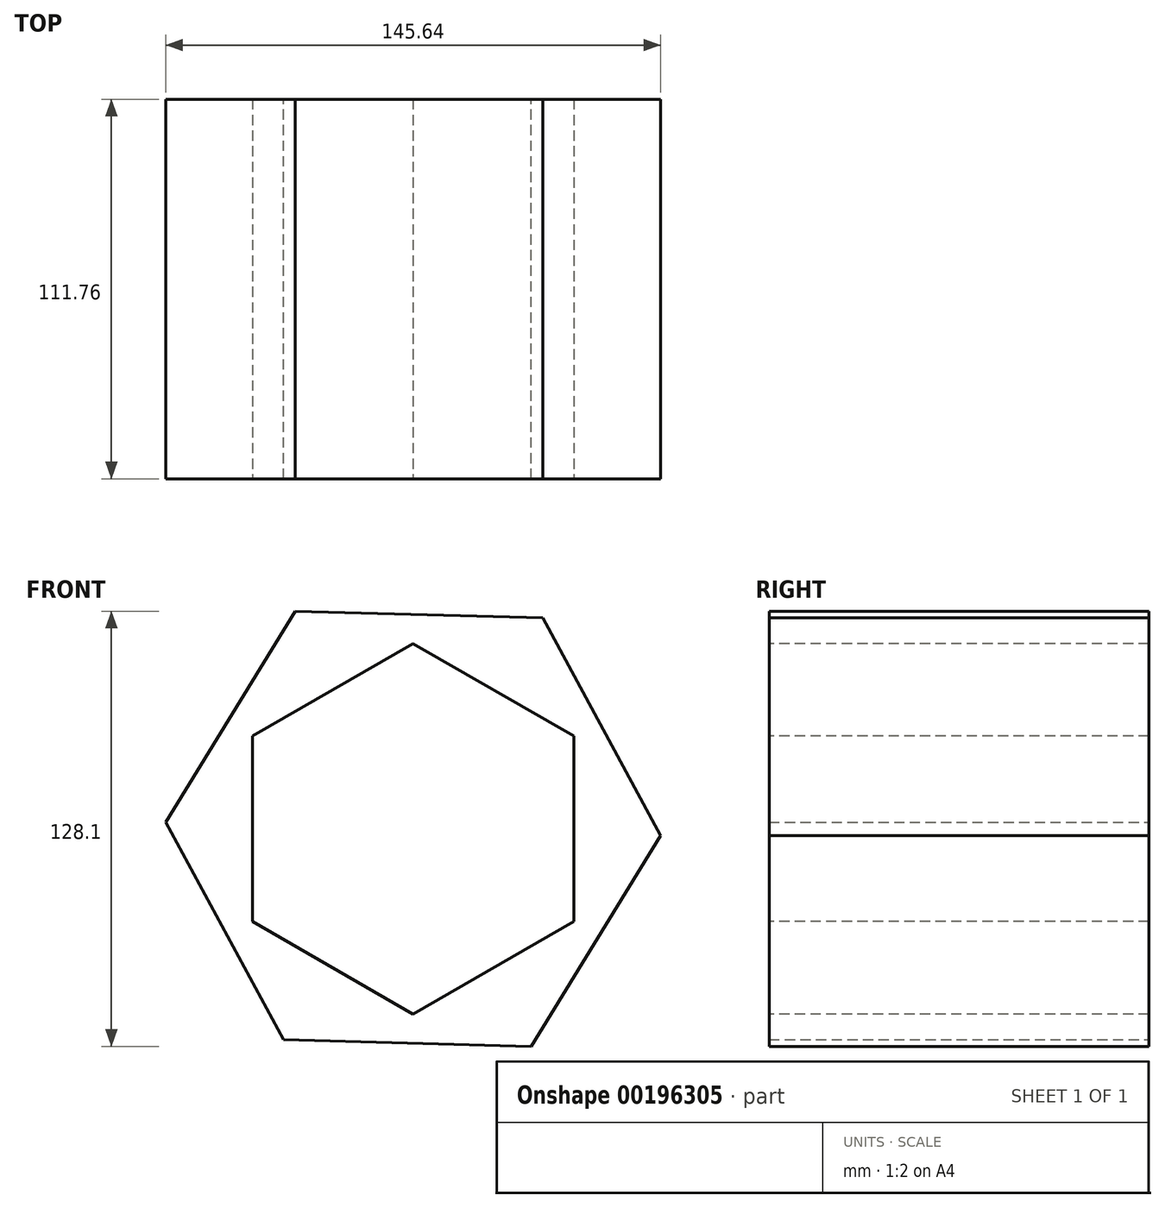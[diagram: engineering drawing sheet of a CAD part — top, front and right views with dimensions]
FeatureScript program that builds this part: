
annotation { "Feature Type Name" : "Feature", "Feature Type Description" : "" }
export const myFeature = defineFeature(function(context is Context, id is Id, definition is map)
    precondition{}
    {
        {
            var Q0;
            Q0=qCreatedBy(makeId("Front.planeOp"),FACE);
            var sketch = newSketch(context, id + "F0", { "sketchPlane" : qUnion([Q0])});
            skCircle(sketch, "E0.cCircle", {"center": v(0, 0) * mm, "radius": 63.09 * mm, "construction": true});
            skLineSegment(sketch, "E0.0", {"start": v(38.11, 62.08) * mm, "end": v(72.82, -1.97) * mm});
            skLineSegment(sketch, "E0.1", {"start": v(72.82, -1.97) * mm, "end": v(34.7, -64.05) * mm});
            skLineSegment(sketch, "E0.2", {"start": v(34.7, -64.05) * mm, "end": v(-38.11, -62.08) * mm});
            skLineSegment(sketch, "E0.3", {"start": v(-38.11, -62.08) * mm, "end": v(-72.82, 1.97) * mm});
            skLineSegment(sketch, "E0.4", {"start": v(-72.82, 1.97) * mm, "end": v(-34.7, 64.05) * mm});
            skLineSegment(sketch, "E0.5", {"start": v(-34.7, 64.05) * mm, "end": v(38.11, 62.08) * mm});
            skPoint(sketch, "E0.0.midPoint", {"position": v(55.47, 30.06) * mm});
            skSolve(sketch);
        }
        {
            var Q0;
            Q0 = qSketchRegion(id + "F0", true);
            extrude(context, id + "F1", {"entities" : qUnion([Q0]), "depth" : 111.76 * mm});
        }
        {
            var Q0;
            Q0=makeQuery(id+"F1.opExtrude","CAP_FACE",FACE,{"disambiguationData":[OSD([sQuery(id+"F0.wireOp",EDGE,"E0.0"),sQuery(id+"F0.wireOp",EDGE,"E0.1"),sQuery(id+"F0.wireOp",EDGE,"E0.2"),sQuery(id+"F0.wireOp",EDGE,"E0.3"),sQuery(id+"F0.wireOp",EDGE,"E0.4"),sQuery(id+"F0.wireOp",EDGE,"E0.5")])],"isStart":false});
            var sketch = newSketch(context, id + "F2", { "sketchPlane" : qUnion([Q0])});
            skCircle(sketch, "E1", {"center": v(0, 0) * mm, "radius": 39.09 * mm});
            skSolve(sketch);
        }
        {
            var Q0;
            Q0=makeQuery(id+"F2.imprint","IMPRINT",FACE,{"disambiguationData":[TD([[makeQuery(id+"F2.imprint","IMPRINT",EDGE,{"derivedFrom":sQuery(id+"F2.wireOp",EDGE,"E1")}),1.0]])]});
            var sketch = newSketch(context, id + "F3", { "sketchPlane" : qUnion([Q0])});
            skCircle(sketch, "E2.cCircle", {"center": v(0, 0) * mm, "radius": 47.25 * mm, "construction": true});
            skLineSegment(sketch, "E2.0", {"start": v(47.25, 27.28) * mm, "end": v(47.25, -27.28) * mm});
            skLineSegment(sketch, "E2.1", {"start": v(47.25, -27.28) * mm, "end": v(0, -54.56) * mm});
            skLineSegment(sketch, "E2.2", {"start": v(0, -54.56) * mm, "end": v(-47.25, -27.28) * mm});
            skLineSegment(sketch, "E2.3", {"start": v(-47.25, -27.28) * mm, "end": v(-47.25, 27.28) * mm});
            skLineSegment(sketch, "E2.4", {"start": v(-47.25, 27.28) * mm, "end": v(0, 54.56) * mm});
            skLineSegment(sketch, "E2.5", {"start": v(0, 54.56) * mm, "end": v(47.25, 27.28) * mm});
            skPoint(sketch, "E2.0.midPoint", {"position": v(47.25, 0) * mm});
            skSolve(sketch);
        }
        {
            var Q0;
            Q0 = qSketchRegion(id + "F3", true);
            extrude(context, id + "F4", {"entities" : qUnion([Q0]), "operationType" : NewBodyOperationType.REMOVE, "oppositeDirection" : true, "depth" : 198.37 * mm});
        }
    });
